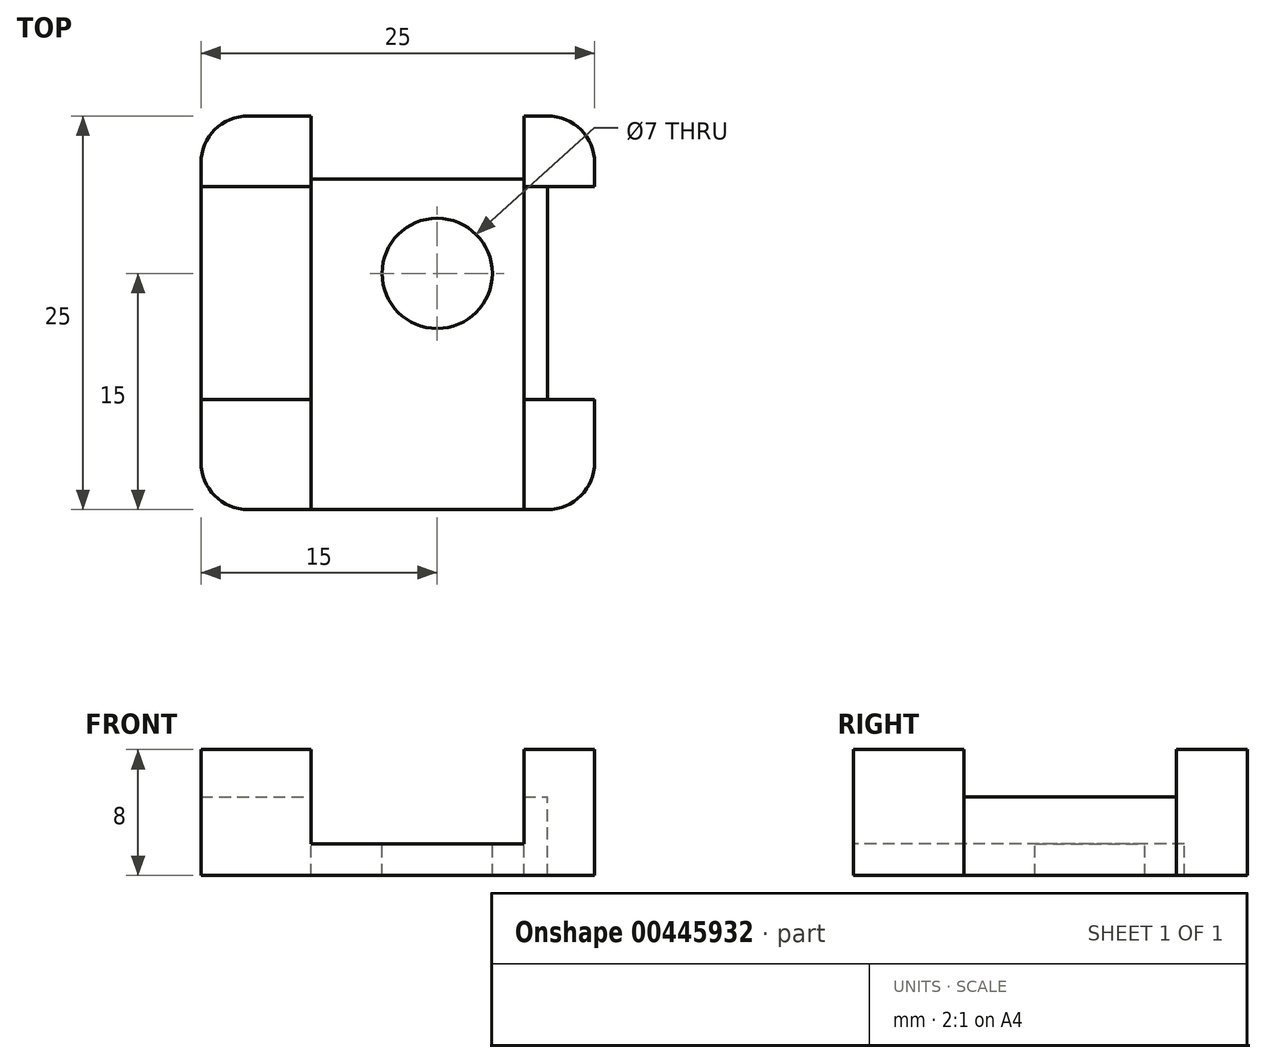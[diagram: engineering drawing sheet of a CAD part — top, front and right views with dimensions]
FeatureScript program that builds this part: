
annotation { "Feature Type Name" : "Feature", "Feature Type Description" : "" }
export const myFeature = defineFeature(function(context is Context, id is Id, definition is map)
    precondition{}
    {
        {
            var Q0;
            Q0=qCreatedBy(makeId("Top.planeOp"),FACE);
            var sketch = newSketch(context, id + "F0", { "sketchPlane" : qUnion([Q0])});
            skLineSegment(sketch, "E0.bottom", {"start": v(-15, -15) * mm, "end": v(10, -15) * mm});
            skLineSegment(sketch, "E0.top", {"start": v(-15, 10) * mm, "end": v(10, 10) * mm});
            skLineSegment(sketch, "E0.left", {"start": v(-15, -15) * mm, "end": v(-15, 10) * mm});
            skLineSegment(sketch, "E0.right", {"start": v(10, -15) * mm, "end": v(10, 10) * mm});
            skPoint(sketch, "E1", {"position": v(0, 0) * mm});
            skSolve(sketch);
        }
        {
            var Q0;
            Q0 = qSketchRegion(id + "F0", true);
            extrude(context, id + "F1", {"entities" : qUnion([Q0]), "depth" : 8 * mm});
        }
        {
            var Q0;
            Q0=makeQuery(id+"F1.opExtrude","CAP_FACE",FACE,{"disambiguationData":[OSD([sQuery(id+"F0.wireOp",EDGE,"E0.bottom"),sQuery(id+"F0.wireOp",EDGE,"E0.top"),sQuery(id+"F0.wireOp",EDGE,"E0.left"),sQuery(id+"F0.wireOp",EDGE,"E0.right")])],"isStart":false});
            var sketch = newSketch(context, id + "F2", { "sketchPlane" : qUnion([Q0])});
            skLineSegment(sketch, "E2.bottom", {"start": v(-8, 10) * mm, "end": v(5.5, 10) * mm});
            skLineSegment(sketch, "E2.top", {"start": v(-8, -15) * mm, "end": v(5.5, -15) * mm});
            skLineSegment(sketch, "E2.left", {"start": v(-8, 10) * mm, "end": v(-8, -15) * mm});
            skLineSegment(sketch, "E2.right", {"start": v(5.5, 10) * mm, "end": v(5.5, -15) * mm});
            skSolve(sketch);
        }
        {
            var Q0;
            Q0 = qSketchRegion(id + "F2", true);
            extrude(context, id + "F3", {"entities" : qUnion([Q0]), "operationType" : NewBodyOperationType.REMOVE, "oppositeDirection" : true, "depth" : 6 * mm});
        }
        {
            var Q0;
            Q0=makeQuery(id+"F1.opExtrude","SWEPT_EDGE",EDGE,{"disambiguationData":[OSD([sQuery(id+"F0.wireOp",EDGE,"E0.bottom"),sQuery(id+"F0.wireOp",EDGE,"E0.right")])]});
            var Q1;
            Q1=makeQuery(id+"F1.opExtrude","SWEPT_EDGE",EDGE,{"disambiguationData":[OSD([sQuery(id+"F0.wireOp",EDGE,"E0.top"),sQuery(id+"F0.wireOp",EDGE,"E0.right")])]});
            var Q2;
            Q2=makeQuery(id+"F1.opExtrude","SWEPT_EDGE",EDGE,{"disambiguationData":[OSD([sQuery(id+"F0.wireOp",EDGE,"E0.top"),sQuery(id+"F0.wireOp",EDGE,"E0.left")])]});
            var Q3;
            Q3=makeQuery(id+"F1.opExtrude","SWEPT_EDGE",EDGE,{"disambiguationData":[OSD([sQuery(id+"F0.wireOp",EDGE,"E0.bottom"),sQuery(id+"F0.wireOp",EDGE,"E0.left")])]});
            fillet(context, id + "F4", {"entities" : qUnion([Q0, Q1, Q2, Q3]), "radius" : 3 * mm, "tangentPropagation" : true, "allowEdgeOverflow" : false});
        }
        {
            var Q0;
            Q0 = qSketchRegion(id + "F2", true);
            extrude(context, id + "F5", {"entities" : qUnion([Q0]), "operationType" : NewBodyOperationType.REMOVE, "oppositeDirection" : true, "depth" : 6 * mm});
        }
        {
            var Q0;
            {var subQ0=sQuery(id+"F0.wireOp",EDGE,"E0.bottom");var subQ1=sQuery(id+"F0.wireOp",EDGE,"E0.top");var subQ2=sQuery(id+"F0.wireOp",EDGE,"E0.left");Q0=makeQuery(id+"F3.boolean.opBoolean","SPLIT",FACE,{"disambiguationData":[TD([makeQuery(id+"F1.opExtrude","SWEPT_FACE",FACE,{"disambiguationData":[OSD([subQ2])]})])],"derivedFrom":makeQuery(id+"F1.opExtrude","CAP_FACE",FACE,{"disambiguationData":[OSD([subQ0,subQ1,subQ2,sQuery(id+"F0.wireOp",EDGE,"E0.right")])],"isStart":false})});}
            var sketch = newSketch(context, id + "F6", { "sketchPlane" : qUnion([Q0])});
            skLineSegment(sketch, "E3.bottom", {"start": v(-15, 5.5) * mm, "end": v(-8, 5.5) * mm});
            skLineSegment(sketch, "E3.top", {"start": v(-15, -8) * mm, "end": v(-8, -8) * mm});
            skLineSegment(sketch, "E3.left", {"start": v(-15, 5.5) * mm, "end": v(-15, -8) * mm});
            skLineSegment(sketch, "E3.right", {"start": v(-8, 5.5) * mm, "end": v(-8, -8) * mm});
            skSolve(sketch);
        }
        {
            var Q0;
            Q0 = qSketchRegion(id + "F6", true);
            extrude(context, id + "F7", {"entities" : qUnion([Q0]), "operationType" : NewBodyOperationType.REMOVE, "oppositeDirection" : true, "depth" : 3 * mm});
        }
        {
            var Q0;
            {var subQ0=sQuery(id+"F0.wireOp",EDGE,"E0.bottom");var subQ1=sQuery(id+"F0.wireOp",EDGE,"E0.right");var subQ2=sQuery(id+"F0.wireOp",EDGE,"E0.top");Q0=makeQuery(id+"F3.boolean.opBoolean","SPLIT",FACE,{"disambiguationData":[TD([makeQuery(id+"F1.opExtrude","SWEPT_FACE",FACE,{"disambiguationData":[OSD([subQ1])]})])],"derivedFrom":makeQuery(id+"F1.opExtrude","CAP_FACE",FACE,{"disambiguationData":[OSD([subQ0,subQ2,sQuery(id+"F0.wireOp",EDGE,"E0.left"),subQ1])],"isStart":false})});}
            var sketch = newSketch(context, id + "F8", { "sketchPlane" : qUnion([Q0])});
            skLineSegment(sketch, "E4.bottom", {"start": v(5.5, 5.5) * mm, "end": v(10, 5.5) * mm});
            skLineSegment(sketch, "E4.top", {"start": v(5.5, -8) * mm, "end": v(10, -8) * mm});
            skLineSegment(sketch, "E4.left", {"start": v(5.5, 5.5) * mm, "end": v(5.5, -8) * mm});
            skLineSegment(sketch, "E4.right", {"start": v(10, 5.5) * mm, "end": v(10, -8) * mm});
            skSolve(sketch);
        }
        {
            var Q0;
            Q0 = qSketchRegion(id + "F8", true);
            extrude(context, id + "F9", {"entities" : qUnion([Q0]), "operationType" : NewBodyOperationType.REMOVE, "oppositeDirection" : true, "depth" : 3 * mm});
        }
        {
            var Q0;
            Q0=makeQuery(id+"F9.boolean.opBoolean","COPY",FACE,{"derivedFrom":makeQuery(id+"F9.opExtrude","CAP_FACE",FACE,{"disambiguationData":[OSD([sQuery(id+"F8.wireOp",EDGE,"E4.bottom"),sQuery(id+"F8.wireOp",EDGE,"E4.top"),sQuery(id+"F8.wireOp",EDGE,"E4.left"),sQuery(id+"F8.wireOp",EDGE,"E4.right")])],"isStart":false})});
            var sketch = newSketch(context, id + "F10", { "sketchPlane" : qUnion([Q0])});
            skLineSegment(sketch, "E5.bottom", {"start": v(10, 5.5) * mm, "end": v(7, 5.5) * mm});
            skLineSegment(sketch, "E5.top", {"start": v(10, -8) * mm, "end": v(7, -8) * mm});
            skLineSegment(sketch, "E5.left", {"start": v(10, 5.5) * mm, "end": v(10, -8) * mm});
            skLineSegment(sketch, "E5.right", {"start": v(7, 5.5) * mm, "end": v(7, -8) * mm});
            skSolve(sketch);
        }
        {
            var Q0;
            Q0 = qSketchRegion(id + "F10", true);
            extrude(context, id + "F11", {"entities" : qUnion([Q0]), "operationType" : NewBodyOperationType.REMOVE, "oppositeDirection" : true, "depth" : 6 * mm});
        }
        {
            var Q0;
            Q0=makeQuery(id+"F3.boolean.opBoolean","COPY",FACE,{"derivedFrom":makeQuery(id+"F3.opExtrude","CAP_FACE",FACE,{"disambiguationData":[OSD([sQuery(id+"F2.wireOp",EDGE,"E2.bottom"),sQuery(id+"F2.wireOp",EDGE,"E2.top"),sQuery(id+"F2.wireOp",EDGE,"E2.left"),sQuery(id+"F2.wireOp",EDGE,"E2.right")])],"isStart":false})});
            var sketch = newSketch(context, id + "F12", { "sketchPlane" : qUnion([Q0])});
            skLineSegment(sketch, "E6.bottom", {"start": v(5.5, 10) * mm, "end": v(-8, 10) * mm});
            skLineSegment(sketch, "E6.top", {"start": v(5.5, 6) * mm, "end": v(-8, 6) * mm});
            skLineSegment(sketch, "E6.left", {"start": v(5.5, 10) * mm, "end": v(5.5, 6) * mm});
            skLineSegment(sketch, "E6.right", {"start": v(-8, 10) * mm, "end": v(-8, 6) * mm});
            skSolve(sketch);
        }
        {
            var Q0;
            Q0 = qSketchRegion(id + "F12", true);
            extrude(context, id + "F13", {"entities" : qUnion([Q0]), "operationType" : NewBodyOperationType.REMOVE, "oppositeDirection" : true, "depth" : 3 * mm});
        }
        {
            var Q0;
            Q0=makeQuery(id+"F1.opExtrude","CAP_FACE",FACE,{"disambiguationData":[OSD([sQuery(id+"F0.wireOp",EDGE,"E0.bottom"),sQuery(id+"F0.wireOp",EDGE,"E0.top"),sQuery(id+"F0.wireOp",EDGE,"E0.left"),sQuery(id+"F0.wireOp",EDGE,"E0.right")])],"isStart":true});
            var sketch = newSketch(context, id + "F14", { "sketchPlane" : qUnion([Q0])});
            skPoint(sketch, "E7", {"position": v(0, 0) * mm});
            skSolve(sketch);
        }
        {
            var Q0;
            Q0=sQuery(id+"F14.wireOp",VERTEX,"E7");
            var Q1;
            Q1=makeQuery(id+"F1.opExtrude","SWEPT_BODY",BODY,{"disambiguationData":[OSD([sQuery(id+"F0.wireOp",EDGE,"E0.bottom"),sQuery(id+"F0.wireOp",EDGE,"E0.top"),sQuery(id+"F0.wireOp",EDGE,"E0.left"),sQuery(id+"F0.wireOp",EDGE,"E0.right")])]});
            hole(context, id + "F15", {"style" : HoleStyle.SIMPLE, "endStyle" : HoleEndStyle.THROUGH, "holeDiameter" : 7 * mm, "isTappedThrough" : true, "tappedDepth" : 12 * mm, "tapClearance" : 3, "locations" : qUnion([Q0]), "scope" : qUnion([Q1]), "startStyle" : HoleStartStyle.SKETCH});
        }
    });
